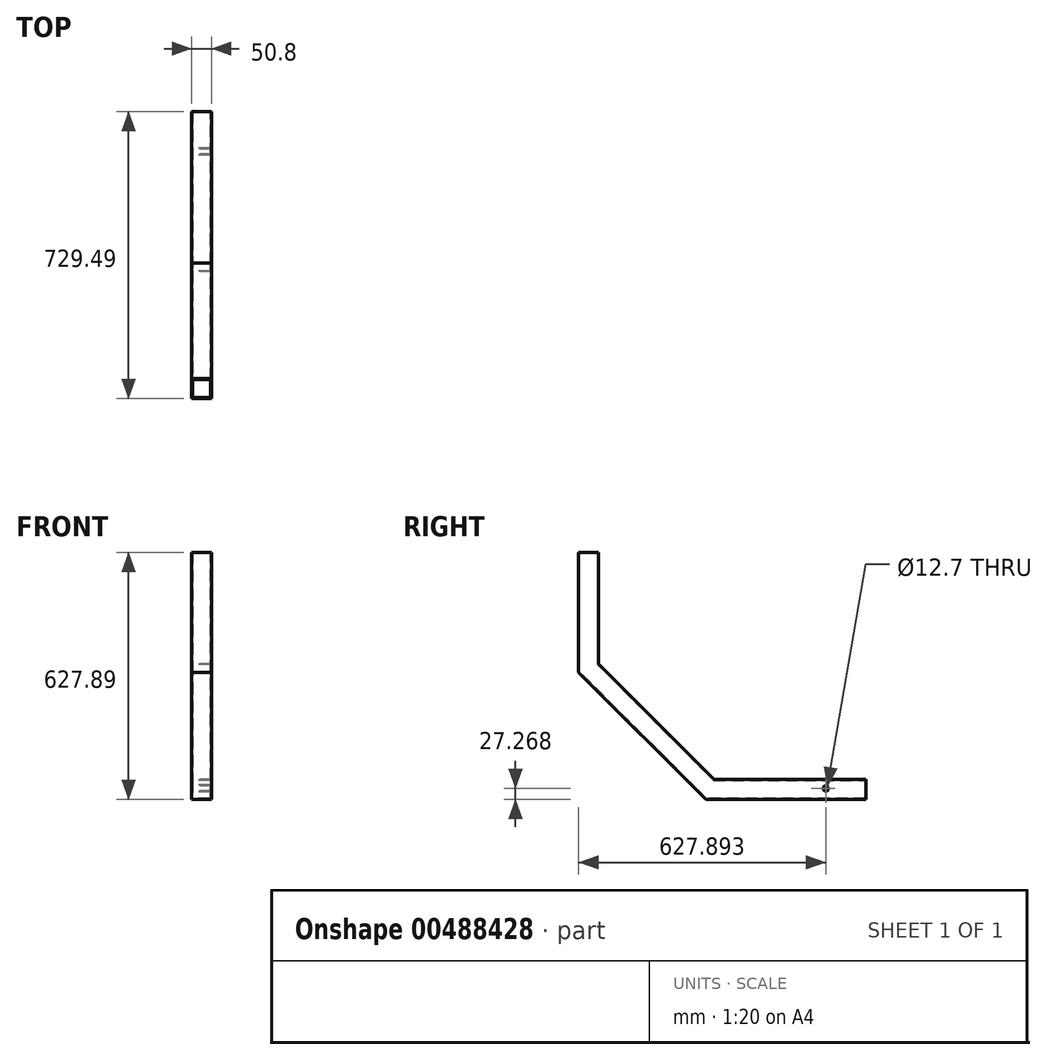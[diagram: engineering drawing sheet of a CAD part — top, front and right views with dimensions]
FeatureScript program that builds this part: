
annotation { "Feature Type Name" : "Feature", "Feature Type Description" : "" }
export const myFeature = defineFeature(function(context is Context, id is Id, definition is map)
    precondition{}
    {
        {
            var Q0;
            Q0=qCreatedBy(makeId("Right.planeOp"),FACE);
            var sketch = newSketch(context, id + "F0", { "sketchPlane" : qUnion([Q0]), "disableImprinting" : false});
            skLineSegment(sketch, "E0", {"start": v(313.92, -209.02) * mm, "end": v(-92.48, -209.02) * mm});
            skLineSegment(sketch, "E1", {"start": v(-92.48, -209.02) * mm, "end": v(-415.57, 114.07) * mm});
            skLineSegment(sketch, "E2", {"start": v(-415.57, 114.07) * mm, "end": v(-415.57, 418.87) * mm});
            skLineSegment(sketch, "E3", {"start": v(-364.77, 418.87) * mm, "end": v(-364.77, 135.1) * mm});
            skLineSegment(sketch, "E4", {"start": v(-364.77, 135.1) * mm, "end": v(-71.45, -158.21) * mm});
            skLineSegment(sketch, "E5", {"start": v(-71.45, -158.21) * mm, "end": v(313.92, -158.22) * mm});
            skLineSegment(sketch, "E6", {"start": v(313.92, -158.22) * mm, "end": v(313.92, -209.02) * mm});
            skLineSegment(sketch, "E7", {"start": v(-364.77, 418.87) * mm, "end": v(-415.57, 418.87) * mm});
            skCircle(sketch, "E8", {"center": v(212.32, -181.75) * mm, "radius": 6.35 * mm});
            skSolve(sketch);
        }
        {
            var Q0;
            Q0=makeQuery(id+"F0.imprint","IMPRINT",FACE,{"disambiguationData":[TD([[makeQuery(id+"F0.imprint","IMPRINT",EDGE,{"derivedFrom":sQuery(id+"F0.wireOp",EDGE,"E0")}),-1.0]])]});
            extrude(context, id + "F1", {"entities" : qUnion([Q0]), "flatOperationType" : FlatOperationType.REMOVE, "offsetDistance" : 25.4 * mm, "depth" : 50.8 * mm, "domain" : OperationDomain.MODEL, "symmetric" : true});
        }
        {
            var Q0;
            Q0=makeQuery(id+"F1.opExtrude","SWEPT_FACE",FACE,{"disambiguationData":[OSD([sQuery(id+"F0.wireOp",EDGE,"E7")])]});
            var Q1;
            Q1=makeQuery(id+"F1.opExtrude","SWEPT_FACE",FACE,{"disambiguationData":[OSD([sQuery(id+"F0.wireOp",EDGE,"E6")])]});
            shell(context, id + "F2", {"entities" : qUnion([Q0, Q1]), "thickness" : 2.54 * mm});
        }
    });
